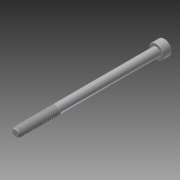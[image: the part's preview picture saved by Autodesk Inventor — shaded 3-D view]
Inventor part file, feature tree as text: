
AUTODESK INVENTOR PART (.ipt)
format: ipt  version: 2014 SP1 (Build 180222100, 222)  size: 501,760 bytes
history: native  units: in
note: dims shown in document units (in); Inventor stores cm internally (conversion verified against a paired STEP export)
features: chamfer x1, other x1, imported_body x1
ambient origin geometry x8: Origin, YZ Plane, XZ Plane, XY Plane, X Axis, Y Axis, Z Axis, Center Point
bodies: Body1 (feature_tree)
feature tree (3):
  chamfer  "Chamfer2"  [1 undecoded]
  other  "91251A0841"
  imported_body  "Base1"
note: 1 required parameter value undecoded (feature->parameter linkage not recoverable at this tier; creation-order binding heuristic only, values carry confidence <= 0.55)
